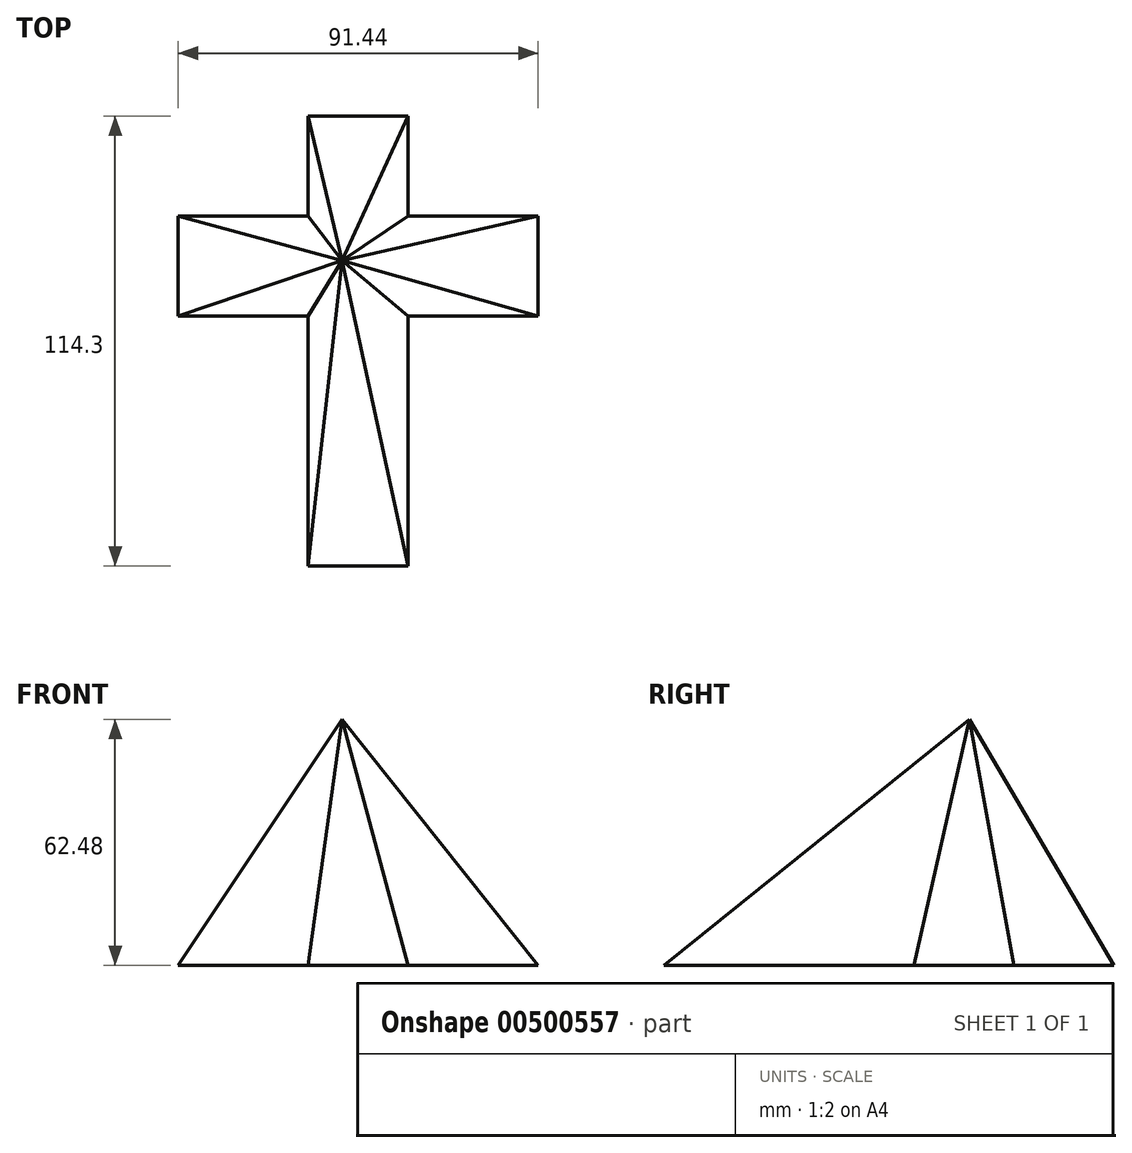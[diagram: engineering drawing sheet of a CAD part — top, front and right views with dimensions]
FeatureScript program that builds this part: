
annotation { "Feature Type Name" : "Feature", "Feature Type Description" : "" }
export const myFeature = defineFeature(function(context is Context, id is Id, definition is map)
    precondition{}
    {
        {
            var Q0;
            Q0=qCreatedBy(makeId("Top.planeOp"),FACE);
            var sketch = newSketch(context, id + "F0", { "sketchPlane" : qUnion([Q0])});
            skLineSegment(sketch, "E0", {"start": v(-14.45, 64.67) * mm, "end": v(10.95, 64.67) * mm});
            skLineSegment(sketch, "E1", {"start": v(10.95, 64.67) * mm, "end": v(10.95, 39.27) * mm});
            skLineSegment(sketch, "E2", {"start": v(10.95, 39.27) * mm, "end": v(43.97, 39.27) * mm});
            skLineSegment(sketch, "E3", {"start": v(43.97, 39.27) * mm, "end": v(43.97, 13.87) * mm});
            skLineSegment(sketch, "E4", {"start": v(43.97, 13.87) * mm, "end": v(10.95, 13.87) * mm});
            skLineSegment(sketch, "E5", {"start": v(10.95, 13.87) * mm, "end": v(10.95, -49.63) * mm});
            skLineSegment(sketch, "E6", {"start": v(10.95, -49.63) * mm, "end": v(-14.45, -49.63) * mm});
            skLineSegment(sketch, "E7", {"start": v(-14.45, -49.63) * mm, "end": v(-14.45, 13.87) * mm});
            skLineSegment(sketch, "E8", {"start": v(-14.45, 13.87) * mm, "end": v(-47.47, 13.87) * mm});
            skLineSegment(sketch, "E9", {"start": v(-47.47, 13.87) * mm, "end": v(-47.47, 39.27) * mm});
            skLineSegment(sketch, "E10", {"start": v(-47.47, 39.27) * mm, "end": v(-14.45, 39.27) * mm});
            skLineSegment(sketch, "E11", {"start": v(-14.45, 39.27) * mm, "end": v(-14.45, 64.67) * mm});
            skSolve(sketch);
        }
        {
            var Q0;
            Q0=qCreatedBy(makeId("Top.planeOp"),FACE);
            cPlane(context, id + "F1", {"entities" : qUnion([Q0]), "cplaneType" : CPlaneType.OFFSET, "offset" : 62.48 * mm, "width" : 152.4 * mm, "height" : 152.4 * mm});
        }
        {
            var Q0;
            Q0=qCreatedBy(id+"F1.planeOp",FACE);
            var sketch = newSketch(context, id + "F2", { "sketchPlane" : qUnion([Q0])});
            skPoint(sketch, "E12", {"position": v(-5.86, 27.99) * mm});
            skSolve(sketch);
        }
        {
            var Q0;
            Q0=sQuery(id+"F2.wireOp",VERTEX,"E12");
            var Q1;
            Q1=makeQuery(id+"F0.imprint","IMPRINT",FACE,{"disambiguationData":[TD([[makeQuery(id+"F0.imprint","IMPRINT",EDGE,{"derivedFrom":sQuery(id+"F0.wireOp",EDGE,"E0")}),-1.0]])]});
            loft(context, id + "F3", {"sheetProfilesArray" : [{ "sheetProfileEntities" : qUnion([Q0]) }, { "sheetProfileEntities" : qUnion([Q1]) }]});
        }
    });
